# Revit family: Security_Video-Intercom_AiPhone_IXG-MK
name_source: partatom
category: Data Devices
units: mm (PartAtom-declared; Revit-internal decimal feet)

## family parameters
Classification Number = 23.85.50.17
Cut with Voids When Loaded = No
Host = Face
Maintain Annotation Orientation = Yes
Part Type = Normal
Room Calculation Point = No
Round Connector Dimension = Use Diameter
Shared = No

## types (1)
- Security_Video-Intercom_AiPhone_IXG-MK
    Black Plastic Trim = Black Plastic
    Body Color = Black Plastic
    Buttons = Silver Trim
    Cost = 0 $
    Default Elevation = 48 "
    Depth = 1.25 "
    Description = IP video guard station
    Door Release Button = Door Release
    Emergency Call Button = Emergency Call Button
    Height = 6.75 "
    Host Width = 24 "
    Manufacturer = AIPHONE
    Model = IXG-MK
    Product Information = https://www.arcat.com
    Screen = Screen
    Talk Button = Talk Button
    URL = https://www.aiphone.com
    Width = 11 "

## geometry (parser evidence)
native form markers: Blend x2, Sweep x4
no freeform markers — native parametric forms only
